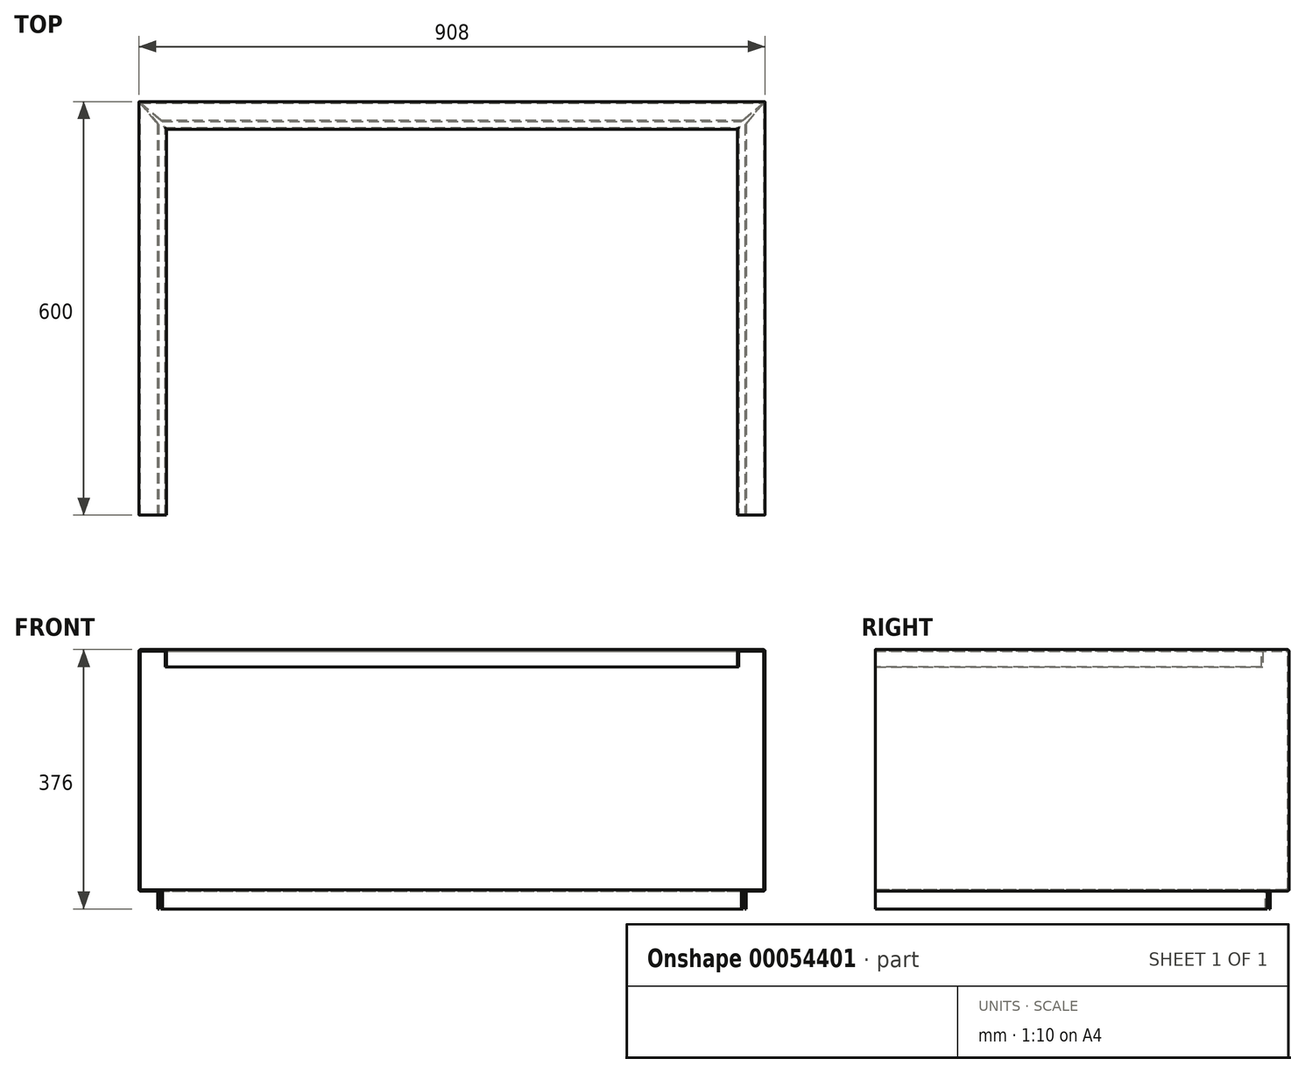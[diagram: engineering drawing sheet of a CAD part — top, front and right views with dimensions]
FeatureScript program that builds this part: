
annotation { "Feature Type Name" : "Feature", "Feature Type Description" : "" }
export const myFeature = defineFeature(function(context is Context, id is Id, definition is map)
    precondition{}
    {
        {
            var Q0;
            Q0=qCreatedBy(makeId("Front.planeOp"),FACE);
            var sketch = newSketch(context, id + "F0", { "sketchPlane" : qUnion([Q0])});
            skLineSegment(sketch, "E0", {"start": v(40, -25) * mm, "end": v(40, 0) * mm});
            skLineSegment(sketch, "E1", {"start": v(40, 0) * mm, "end": v(0, 0) * mm});
            skLineSegment(sketch, "E2", {"start": v(0, 0) * mm, "end": v(0, -350) * mm});
            skLineSegment(sketch, "E3", {"start": v(0, -350) * mm, "end": v(27, -350) * mm});
            skLineSegment(sketch, "E4", {"start": v(27, -350) * mm, "end": v(27, -376) * mm});
            skLineSegment(sketch, "E5.0", {"start": v(29, -348) * mm, "end": v(29, -376) * mm});
            skLineSegment(sketch, "E5.1", {"start": v(38, -25) * mm, "end": v(38, -2) * mm});
            skLineSegment(sketch, "E5.2", {"start": v(38, -2) * mm, "end": v(2, -2) * mm});
            skLineSegment(sketch, "E5.3", {"start": v(2, -2) * mm, "end": v(2, -348) * mm});
            skLineSegment(sketch, "E5.4", {"start": v(2, -348) * mm, "end": v(29, -348) * mm});
            skLineSegment(sketch, "E6", {"start": v(38, -25) * mm, "end": v(40, -25) * mm});
            skLineSegment(sketch, "E7", {"start": v(27, -376) * mm, "end": v(29, -376) * mm});
            skSolve(sketch);
        }
        {
            var Q0;
            Q0=qCreatedBy(makeId("Top.planeOp"),FACE);
            var sketch = newSketch(context, id + "F1", { "sketchPlane" : qUnion([Q0])});
            skLineSegment(sketch, "E8", {"start": v(0, 0) * mm, "end": v(0, 600) * mm});
            skLineSegment(sketch, "E9", {"start": v(0, 600) * mm, "end": v(908, 600) * mm});
            skLineSegment(sketch, "E10", {"start": v(908, 600) * mm, "end": v(908, 0) * mm});
            skSolve(sketch);
        }
        {
            var Q0;
            Q0=qSketchRegion(id+"F0",true);
            var Q1;
            Q1=qConstructionFilter(qBodyType(qCreatedBy(id+"F1",EDGE),BodyType.WIRE),ConstructionObject.NO);
            sweep(context, id + "F2", {"profiles" : qUnion([Q0]), "path" : qUnion([Q1])});
        }
        {
            var Q0;
            Q0=makeQuery(id+"F2.opSweep","SWEPT_FACE",FACE,{"disambiguationData":[OSD([sQuery(id+"F0.wireOp",EDGE,"E5.4"),sQuery(id+"F1.wireOp",EDGE,"E8")])]});
            var sketch = newSketch(context, id + "F3", { "sketchPlane" : qUnion([Q0])});
            skLineSegment(sketch, "E11", {"start": v(2, 598) * mm, "end": v(29, 565.82) * mm});
            skLineSegment(sketch, "E12", {"start": v(29, 565.82) * mm, "end": v(34.18, 571) * mm});
            skLineSegment(sketch, "E13", {"start": v(34.18, 571) * mm, "end": v(2, 598) * mm});
            skLineSegment(sketch, "E14", {"start": v(906, 598) * mm, "end": v(879, 565.82) * mm});
            skLineSegment(sketch, "E15", {"start": v(879, 565.82) * mm, "end": v(873.82, 571) * mm});
            skLineSegment(sketch, "E16", {"start": v(873.82, 571) * mm, "end": v(906, 598) * mm});
            skSolve(sketch);
        }
        {
            var Q0;
            {var subQ0=sQuery(id+"F3.wireOp",EDGE,"E14");Q0=makeQuery(id+"F3.imprint","IMPRINT",FACE,{"disambiguationData":[TD([[makeQuery(id+"F3.imprint","IMPRINT",EDGE,{"derivedFrom":subQ0}),-1.0]])]});}
            var Q1;
            {var subQ0=sQuery(id+"F3.wireOp",EDGE,"E11");Q1=makeQuery(id+"F3.imprint","IMPRINT",FACE,{"disambiguationData":[TD([[makeQuery(id+"F3.imprint","IMPRINT",EDGE,{"derivedFrom":subQ0}),1.0]])]});}
            extrude(context, id + "F4", {"entities" : qUnion([Q0, Q1]), "operationType" : NewBodyOperationType.REMOVE, "oppositeDirection" : true, "depth" : 30 * mm});
        }
        {
            var Q0;
            Q0=makeQuery(id+"F2.opSweep","SWEPT_EDGE",EDGE,{"disambiguationData":[OSD([sQuery(id+"F0.wireOp",EDGE,"E0"),sQuery(id+"F0.wireOp",EDGE,"E1"),sQuery(id+"F1.wireOp",EDGE,"E8")])]});
            var Q1;
            Q1=makeQuery(id+"F2.opSweep","SWEPT_EDGE",EDGE,{"disambiguationData":[OSD([sQuery(id+"F0.wireOp",EDGE,"E1"),sQuery(id+"F0.wireOp",EDGE,"E2"),sQuery(id+"F1.wireOp",EDGE,"E8")])]});
            var Q2;
            Q2=makeQuery(id+"F2.opSweep","SWEPT_EDGE",EDGE,{"disambiguationData":[OSD([sQuery(id+"F0.wireOp",EDGE,"E0"),sQuery(id+"F0.wireOp",EDGE,"E1"),sQuery(id+"F1.wireOp",EDGE,"E9")])]});
            var Q3;
            Q3=makeQuery(id+"F2.opSweep","SWEPT_EDGE",EDGE,{"disambiguationData":[OSD([sQuery(id+"F0.wireOp",EDGE,"E1"),sQuery(id+"F0.wireOp",EDGE,"E2"),sQuery(id+"F1.wireOp",EDGE,"E9")])]});
            var Q4;
            Q4=makeQuery(id+"F2.opSweep","SWEPT_EDGE",EDGE,{"disambiguationData":[OSD([sQuery(id+"F0.wireOp",EDGE,"E0"),sQuery(id+"F0.wireOp",EDGE,"E1"),sQuery(id+"F1.wireOp",EDGE,"E10")])]});
            var Q5;
            Q5=makeQuery(id+"F2.opSweep","SWEPT_EDGE",EDGE,{"disambiguationData":[OSD([sQuery(id+"F0.wireOp",EDGE,"E1"),sQuery(id+"F0.wireOp",EDGE,"E2"),sQuery(id+"F1.wireOp",EDGE,"E10")])]});
            var Q6;
            Q6=makeQuery(id+"F2.opSweep","SWEPT_EDGE",EDGE,{"disambiguationData":[OSD([sQuery(id+"F0.wireOp",EDGE,"E5.0"),sQuery(id+"F0.wireOp",EDGE,"E5.4"),sQuery(id+"F1.wireOp",EDGE,"E8")])]});
            var Q7;
            Q7=makeQuery(id+"F2.opSweep","SWEPT_EDGE",EDGE,{"disambiguationData":[OSD([sQuery(id+"F0.wireOp",EDGE,"E5.3"),sQuery(id+"F0.wireOp",EDGE,"E5.4"),sQuery(id+"F1.wireOp",EDGE,"E8")])]});
            var Q8;
            Q8=makeQuery(id+"F2.opSweep","SWEPT_EDGE",EDGE,{"disambiguationData":[OSD([sQuery(id+"F0.wireOp",EDGE,"E5.0"),sQuery(id+"F0.wireOp",EDGE,"E5.4"),sQuery(id+"F1.wireOp",EDGE,"E9")])]});
            var Q9;
            Q9=makeQuery(id+"F2.opSweep","SWEPT_EDGE",EDGE,{"disambiguationData":[OSD([sQuery(id+"F0.wireOp",EDGE,"E5.3"),sQuery(id+"F0.wireOp",EDGE,"E5.4"),sQuery(id+"F1.wireOp",EDGE,"E9")])]});
            var Q10;
            Q10=makeQuery(id+"F2.opSweep","SWEPT_EDGE",EDGE,{"disambiguationData":[OSD([sQuery(id+"F0.wireOp",EDGE,"E5.0"),sQuery(id+"F0.wireOp",EDGE,"E5.4"),sQuery(id+"F1.wireOp",EDGE,"E10")])]});
            var Q11;
            Q11=makeQuery(id+"F2.opSweep","SWEPT_EDGE",EDGE,{"disambiguationData":[OSD([sQuery(id+"F0.wireOp",EDGE,"E5.3"),sQuery(id+"F0.wireOp",EDGE,"E5.4"),sQuery(id+"F1.wireOp",EDGE,"E10")])]});
            var Q12;
            Q12=makeQuery(id+"F2.opSweep","SWEPT_EDGE",EDGE,{"disambiguationData":[OSD([sQuery(id+"F0.wireOp",EDGE,"E2"),sQuery(id+"F0.wireOp",EDGE,"E3"),sQuery(id+"F1.wireOp",EDGE,"E8")])]});
            var Q13;
            Q13=makeQuery(id+"F2.opSweep","SWEPT_EDGE",EDGE,{"disambiguationData":[OSD([sQuery(id+"F0.wireOp",EDGE,"E3"),sQuery(id+"F0.wireOp",EDGE,"E4"),sQuery(id+"F1.wireOp",EDGE,"E8")])]});
            var Q14;
            Q14=makeQuery(id+"F2.opSweep","SWEPT_EDGE",EDGE,{"disambiguationData":[OSD([sQuery(id+"F0.wireOp",EDGE,"E2"),sQuery(id+"F0.wireOp",EDGE,"E3"),sQuery(id+"F1.wireOp",EDGE,"E9")])]});
            var Q15;
            Q15=makeQuery(id+"F2.opSweep","SWEPT_EDGE",EDGE,{"disambiguationData":[OSD([sQuery(id+"F0.wireOp",EDGE,"E3"),sQuery(id+"F0.wireOp",EDGE,"E4"),sQuery(id+"F1.wireOp",EDGE,"E9")])]});
            var Q16;
            Q16=makeQuery(id+"F2.opSweep","SWEPT_EDGE",EDGE,{"disambiguationData":[OSD([sQuery(id+"F0.wireOp",EDGE,"E3"),sQuery(id+"F0.wireOp",EDGE,"E4"),sQuery(id+"F1.wireOp",EDGE,"E10")])]});
            var Q17;
            Q17=makeQuery(id+"F2.opSweep","SWEPT_EDGE",EDGE,{"disambiguationData":[OSD([sQuery(id+"F0.wireOp",EDGE,"E2"),sQuery(id+"F0.wireOp",EDGE,"E3"),sQuery(id+"F1.wireOp",EDGE,"E10")])]});
            var Q18;
            Q18=makeQuery(id+"F2.opSweep","SWEPT_EDGE",EDGE,{"disambiguationData":[OSD([sQuery(id+"F0.wireOp",EDGE,"E5.1"),sQuery(id+"F0.wireOp",EDGE,"E5.2"),sQuery(id+"F1.wireOp",EDGE,"E10")])]});
            var Q19;
            Q19=makeQuery(id+"F2.opSweep","SWEPT_EDGE",EDGE,{"disambiguationData":[OSD([sQuery(id+"F0.wireOp",EDGE,"E5.2"),sQuery(id+"F0.wireOp",EDGE,"E5.3"),sQuery(id+"F1.wireOp",EDGE,"E10")])]});
            var Q20;
            Q20=makeQuery(id+"F2.opSweep","SWEPT_EDGE",EDGE,{"disambiguationData":[OSD([sQuery(id+"F0.wireOp",EDGE,"E5.2"),sQuery(id+"F0.wireOp",EDGE,"E5.3"),sQuery(id+"F1.wireOp",EDGE,"E9")])]});
            var Q21;
            Q21=makeQuery(id+"F2.opSweep","SWEPT_EDGE",EDGE,{"disambiguationData":[OSD([sQuery(id+"F0.wireOp",EDGE,"E5.1"),sQuery(id+"F0.wireOp",EDGE,"E5.2"),sQuery(id+"F1.wireOp",EDGE,"E8")])]});
            var Q22;
            Q22=makeQuery(id+"F2.opSweep","SWEPT_EDGE",EDGE,{"disambiguationData":[OSD([sQuery(id+"F0.wireOp",EDGE,"E5.2"),sQuery(id+"F0.wireOp",EDGE,"E5.3"),sQuery(id+"F1.wireOp",EDGE,"E8")])]});
            var Q23;
            Q23=makeQuery(id+"F2.opSweep","SWEPT_EDGE",EDGE,{"disambiguationData":[OSD([sQuery(id+"F0.wireOp",EDGE,"E5.1"),sQuery(id+"F0.wireOp",EDGE,"E5.2"),sQuery(id+"F1.wireOp",EDGE,"E9")])]});
            fillet(context, id + "F5", {"entities" : qUnion([Q0, Q1, Q2, Q3, Q4, Q5, Q6, Q7, Q8, Q9, Q10, Q11, Q12, Q13, Q14, Q15, Q16, Q17, Q18, Q19, Q20, Q21, Q22, Q23]), "radius" : 2 * mm, "tangentPropagation" : true, "allowEdgeOverflow" : false});
        }
    });
